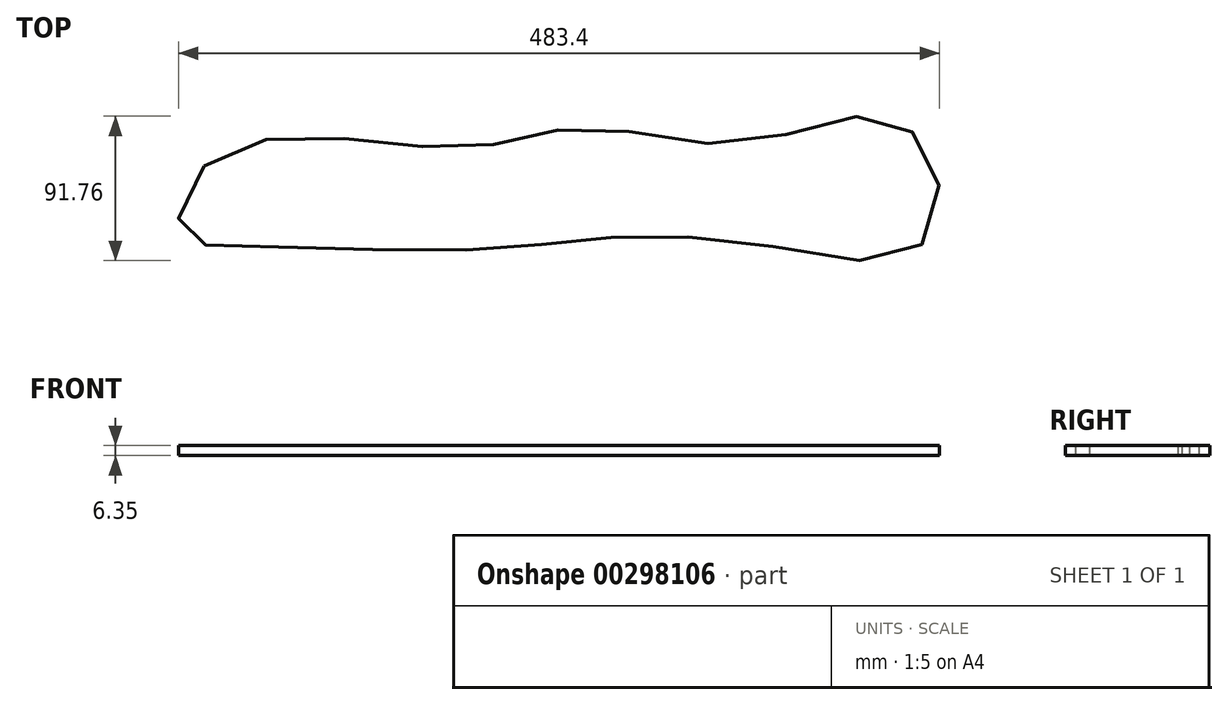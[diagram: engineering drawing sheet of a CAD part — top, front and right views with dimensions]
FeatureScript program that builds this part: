
annotation { "Feature Type Name" : "Feature", "Feature Type Description" : "" }
export const myFeature = defineFeature(function(context is Context, id is Id, definition is map)
    precondition{}
    {
        {
            var Q0;
            Q0=qCreatedBy(makeId("Front.planeOp"),FACE);
            var sketch = newSketch(context, id + "F0", { "sketchPlane" : qUnion([Q0])});
            skLineSegment(sketch, "E0", {"start": v(-123.6, 29.15) * mm, "end": v(-1.44, 0.34) * mm});
            skLineSegment(sketch, "E1", {"start": v(1.48, 0) * mm, "end": v(584.2, 0) * mm});
            skPoint(sketch, "E2.visualSharp", {"position": v(0, 0) * mm});
            skArc(sketch, "E2.filletArc", {"start": v(-1.44, 0.34) * mm, "mid": v(0, 0.09) * mm, "end": v(1.48, 0) * mm});
            skLineSegment(sketch, "E3.0", {"start": v(-125.07, 22.97) * mm, "end": v(-2.9, -5.84) * mm});
            skLineSegment(sketch, "E4.0", {"start": v(1.48, -6.35) * mm, "end": v(584.2, -6.35) * mm});
            skLineSegment(sketch, "E5", {"start": v(-123.6, 29.15) * mm, "end": v(-125.07, 22.97) * mm});
            skLineSegment(sketch, "E6", {"start": v(-2.9, -5.84) * mm, "end": v(1.48, -6.35) * mm});
            skLineSegment(sketch, "E7", {"start": v(584.2, -6.35) * mm, "end": v(584.2, 0) * mm});
            skSolve(sketch);
        }
        {
            var Q0;
            Q0=makeQuery(id+"F0.imprint","IMPRINT",FACE,{"disambiguationData":[TD([[makeQuery(id+"F0.imprint","IMPRINT",EDGE,{"derivedFrom":sQuery(id+"F0.wireOp",EDGE,"E0")}),-1.0]])]});
            extrude(context, id + "F1", {"entities" : qUnion([Q0]), "depth" : 190.5 * mm});
        }
        {
            var Q0;
            Q0=qCreatedBy(makeId("Top.planeOp"),FACE);
            var sketch = newSketch(context, id + "F2", { "sketchPlane" : qUnion([Q0])});
            skFitSpline(sketch, "E8", {"points": [v(93.61, -73.82) * mm, v(171.55, -55.63) * mm, v(265.5, -61.7) * mm, v(335.65, -49.14) * mm, v(432.64, -59.53) * mm, v(517.07, -42.21) * mm, v(557.33, -72.09) * mm, v(545.21, -127.08) * mm, v(449.09, -124.05) * mm, v(346.04, -119.72) * mm, v(261.17, -127.08) * mm, v(124.35, -124.91) * mm, v(78.89, -115.82) * mm, v(93.61, -73.82) * mm]});
            skSolve(sketch);
        }
        {
            var Q0;
            Q0=makeQuery(id+"F2.imprint","IMPRINT",FACE,{"disambiguationData":[TD([[makeQuery(id+"F2.imprint","IMPRINT",EDGE,{"derivedFrom":sQuery(id+"F2.wireOp",EDGE,"E8")}),-1.0]])]});
            extrude(context, id + "F3", {"entities" : qUnion([Q0]), "operationType" : NewBodyOperationType.INTERSECT, "oppositeDirection" : true, "depth" : 25.4 * mm});
        }
    });
